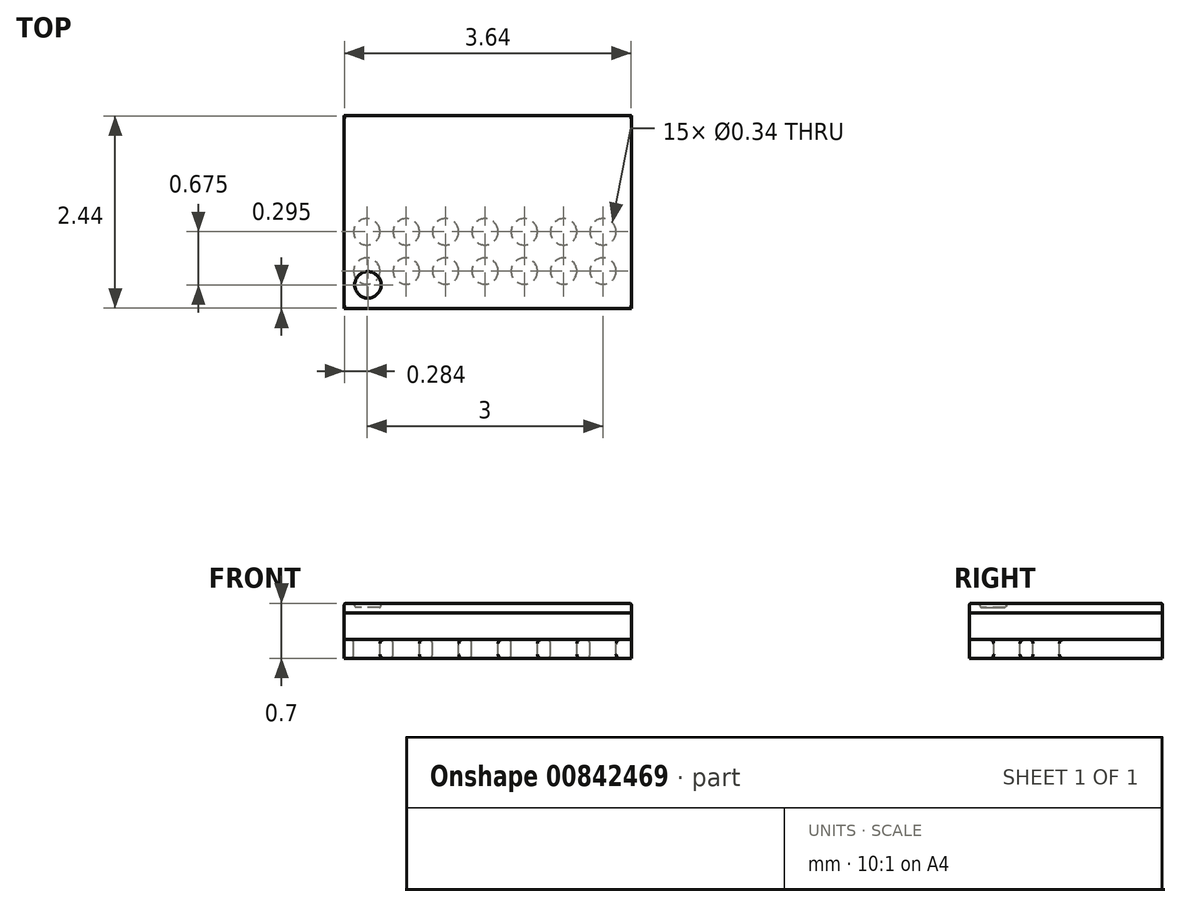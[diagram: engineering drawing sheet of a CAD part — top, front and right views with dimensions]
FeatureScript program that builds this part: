
annotation { "Feature Type Name" : "Feature", "Feature Type Description" : "" }
export const myFeature = defineFeature(function(context is Context, id is Id, definition is map)
    precondition{}
    {
        {
            var Q0;
            Q0=qCreatedBy(makeId("Top.planeOp"),FACE);
            var sketch = newSketch(context, id + "F0", { "sketchPlane" : qUnion([Q0])});
            skLineSegment(sketch, "E0.bottom", {"start": v(-1.82, 1.22) * mm, "end": v(1.82, 1.22) * mm});
            skLineSegment(sketch, "E0.top", {"start": v(-1.82, -1.22) * mm, "end": v(1.82, -1.22) * mm});
            skLineSegment(sketch, "E0.left", {"start": v(-1.82, 1.22) * mm, "end": v(-1.82, -1.22) * mm});
            skLineSegment(sketch, "E0.right", {"start": v(1.82, 1.22) * mm, "end": v(1.82, -1.22) * mm});
            skPoint(sketch, "E0.middle", {"position": v(0, 0) * mm});
            skSolve(sketch);
        }
        {
            var Q0;
            Q0=makeQuery(id+"F0.imprint","IMPRINT",FACE,{"disambiguationData":[TD([[makeQuery(id+"F0.imprint","IMPRINT",EDGE,{"derivedFrom":sQuery(id+"F0.wireOp",EDGE,"E0.bottom")}),-1.0]])]});
            extrude(context, id + "F1", {"entities" : qUnion([Q0]), "depth" : 0.34 * mm, "offsetDistance" : 25 * mm});
        }
        {
            var Q0;
            Q0=makeQuery(id+"F1.opExtrude","CAP_FACE",FACE,{"disambiguationData":[OSD([sQuery(id+"F0.wireOp",EDGE,"E0.bottom"),sQuery(id+"F0.wireOp",EDGE,"E0.top"),sQuery(id+"F0.wireOp",EDGE,"E0.left"),sQuery(id+"F0.wireOp",EDGE,"E0.right")])],"isStart":false});
            extrude(context, id + "F2", {"entities" : qUnion([Q0]), "depth" : 0.12 * mm, "offsetDistance" : 25 * mm});
        }
        {
            var Q0;
            Q0=makeQuery(id+"F1.opExtrude","CAP_FACE",FACE,{"disambiguationData":[OSD([sQuery(id+"F0.wireOp",EDGE,"E0.bottom"),sQuery(id+"F0.wireOp",EDGE,"E0.top"),sQuery(id+"F0.wireOp",EDGE,"E0.left"),sQuery(id+"F0.wireOp",EDGE,"E0.right")])],"isStart":true});
            var sketch = newSketch(context, id + "F3", { "sketchPlane" : qUnion([Q0])});
            skCircle(sketch, "E1", {"center": v(1.46, -0.75) * mm, "radius": 0.17 * mm});
            skCircle(sketch, "E2", {"center": v(1.46, -0.25) * mm, "radius": 0.17 * mm});
            skCircle(sketch, "E3", {"center": v(0.96, -0.75) * mm, "radius": 0.17 * mm});
            skCircle(sketch, "E4", {"center": v(0.96, -0.25) * mm, "radius": 0.17 * mm});
            skCircle(sketch, "E5", {"center": v(0.46, -0.75) * mm, "radius": 0.17 * mm});
            skCircle(sketch, "E6", {"center": v(0.46, -0.25) * mm, "radius": 0.17 * mm});
            skCircle(sketch, "E7", {"center": v(-0.04, -0.75) * mm, "radius": 0.17 * mm});
            skCircle(sketch, "E8", {"center": v(-0.04, -0.25) * mm, "radius": 0.17 * mm});
            skCircle(sketch, "E9", {"center": v(-0.54, -0.75) * mm, "radius": 0.17 * mm});
            skCircle(sketch, "E10", {"center": v(-0.54, -0.25) * mm, "radius": 0.17 * mm});
            skCircle(sketch, "E11", {"center": v(-1.04, -0.75) * mm, "radius": 0.17 * mm});
            skCircle(sketch, "E12", {"center": v(-1.04, -0.25) * mm, "radius": 0.17 * mm});
            skCircle(sketch, "E13", {"center": v(-1.54, -0.75) * mm, "radius": 0.17 * mm});
            skCircle(sketch, "E14", {"center": v(-1.54, -0.25) * mm, "radius": 0.17 * mm});
            skCircle(sketch, "E15.MirrorC", {"center": v(-1.54, 0.25) * mm, "radius": 0.17 * mm});
            skCircle(sketch, "E16.MirrorC", {"center": v(-1.04, 0.25) * mm, "radius": 0.17 * mm});
            skCircle(sketch, "E17.MirrorC", {"center": v(-0.54, 0.25) * mm, "radius": 0.17 * mm});
            skCircle(sketch, "E18.MirrorC", {"center": v(-0.04, 0.25) * mm, "radius": 0.17 * mm});
            skCircle(sketch, "E19.MirrorC", {"center": v(0.46, 0.25) * mm, "radius": 0.17 * mm});
            skCircle(sketch, "E20.MirrorC", {"center": v(0.96, 0.25) * mm, "radius": 0.17 * mm});
            skCircle(sketch, "E21.MirrorC", {"center": v(1.46, 0.25) * mm, "radius": 0.17 * mm});
            skCircle(sketch, "E22.MirrorC", {"center": v(1.46, 0.75) * mm, "radius": 0.17 * mm});
            skCircle(sketch, "E23.MirrorC", {"center": v(0.96, 0.75) * mm, "radius": 0.17 * mm});
            skCircle(sketch, "E24.MirrorC", {"center": v(0.46, 0.75) * mm, "radius": 0.17 * mm});
            skCircle(sketch, "E25.MirrorC", {"center": v(-0.04, 0.75) * mm, "radius": 0.17 * mm});
            skCircle(sketch, "E26.MirrorC", {"center": v(-0.54, 0.75) * mm, "radius": 0.17 * mm});
            skCircle(sketch, "E27.MirrorC", {"center": v(-1.04, 0.75) * mm, "radius": 0.17 * mm});
            skCircle(sketch, "E28.MirrorC", {"center": v(-1.54, 0.75) * mm, "radius": 0.17 * mm});
            skSolve(sketch);
        }
        {
            var Q0;
            Q0=makeQuery(id+"F3.imprint","IMPRINT",FACE,{"disambiguationData":[TD([[makeQuery(id+"F3.imprint","IMPRINT",EDGE,{"derivedFrom":sQuery(id+"F3.wireOp",EDGE,"E1")}),1.0]])]});
            var Q1;
            Q1=makeQuery(id+"F3.imprint","IMPRINT",FACE,{"disambiguationData":[TD([[makeQuery(id+"F3.imprint","IMPRINT",EDGE,{"derivedFrom":sQuery(id+"F3.wireOp",EDGE,"E2")}),1.0]])]});
            var Q2;
            Q2=makeQuery(id+"F3.imprint","IMPRINT",FACE,{"disambiguationData":[TD([[makeQuery(id+"F3.imprint","IMPRINT",EDGE,{"derivedFrom":sQuery(id+"F3.wireOp",EDGE,"E3")}),1.0]])]});
            var Q3;
            Q3=makeQuery(id+"F3.imprint","IMPRINT",FACE,{"disambiguationData":[TD([[makeQuery(id+"F3.imprint","IMPRINT",EDGE,{"derivedFrom":sQuery(id+"F3.wireOp",EDGE,"E4")}),1.0]])]});
            var Q4;
            Q4=makeQuery(id+"F3.imprint","IMPRINT",FACE,{"disambiguationData":[TD([[makeQuery(id+"F3.imprint","IMPRINT",EDGE,{"derivedFrom":sQuery(id+"F3.wireOp",EDGE,"E5")}),1.0]])]});
            var Q5;
            Q5=makeQuery(id+"F3.imprint","IMPRINT",FACE,{"disambiguationData":[TD([[makeQuery(id+"F3.imprint","IMPRINT",EDGE,{"derivedFrom":sQuery(id+"F3.wireOp",EDGE,"E6")}),1.0]])]});
            var Q6;
            Q6=makeQuery(id+"F3.imprint","IMPRINT",FACE,{"disambiguationData":[TD([[makeQuery(id+"F3.imprint","IMPRINT",EDGE,{"derivedFrom":sQuery(id+"F3.wireOp",EDGE,"E7")}),1.0]])]});
            var Q7;
            Q7=makeQuery(id+"F3.imprint","IMPRINT",FACE,{"disambiguationData":[TD([[makeQuery(id+"F3.imprint","IMPRINT",EDGE,{"derivedFrom":sQuery(id+"F3.wireOp",EDGE,"E8")}),1.0]])]});
            var Q8;
            Q8=makeQuery(id+"F3.imprint","IMPRINT",FACE,{"disambiguationData":[TD([[makeQuery(id+"F3.imprint","IMPRINT",EDGE,{"derivedFrom":sQuery(id+"F3.wireOp",EDGE,"E9")}),1.0]])]});
            var Q9;
            Q9=makeQuery(id+"F3.imprint","IMPRINT",FACE,{"disambiguationData":[TD([[makeQuery(id+"F3.imprint","IMPRINT",EDGE,{"derivedFrom":sQuery(id+"F3.wireOp",EDGE,"E10")}),1.0]])]});
            var Q10;
            Q10=makeQuery(id+"F3.imprint","IMPRINT",FACE,{"disambiguationData":[TD([[makeQuery(id+"F3.imprint","IMPRINT",EDGE,{"derivedFrom":sQuery(id+"F3.wireOp",EDGE,"E11")}),1.0]])]});
            var Q11;
            Q11=makeQuery(id+"F3.imprint","IMPRINT",FACE,{"disambiguationData":[TD([[makeQuery(id+"F3.imprint","IMPRINT",EDGE,{"derivedFrom":sQuery(id+"F3.wireOp",EDGE,"E12")}),1.0]])]});
            var Q12;
            Q12=makeQuery(id+"F3.imprint","IMPRINT",FACE,{"disambiguationData":[TD([[makeQuery(id+"F3.imprint","IMPRINT",EDGE,{"derivedFrom":sQuery(id+"F3.wireOp",EDGE,"E13")}),1.0]])]});
            var Q13;
            Q13=makeQuery(id+"F3.imprint","IMPRINT",FACE,{"disambiguationData":[TD([[makeQuery(id+"F3.imprint","IMPRINT",EDGE,{"derivedFrom":sQuery(id+"F3.wireOp",EDGE,"E14")}),1.0]])]});
            var Q14;
            Q14=makeQuery(id+"F3.imprint","IMPRINT",FACE,{"disambiguationData":[TD([[makeQuery(id+"F3.imprint","IMPRINT",EDGE,{"derivedFrom":sQuery(id+"F3.wireOp",EDGE,"E15.MirrorC")}),-1.0]])]});
            var Q15;
            Q15=makeQuery(id+"F3.imprint","IMPRINT",FACE,{"disambiguationData":[TD([[makeQuery(id+"F3.imprint","IMPRINT",EDGE,{"derivedFrom":sQuery(id+"F3.wireOp",EDGE,"E28.MirrorC")}),-1.0]])]});
            var Q16;
            Q16=makeQuery(id+"F3.imprint","IMPRINT",FACE,{"disambiguationData":[TD([[makeQuery(id+"F3.imprint","IMPRINT",EDGE,{"derivedFrom":sQuery(id+"F3.wireOp",EDGE,"E27.MirrorC")}),-1.0]])]});
            var Q17;
            Q17=makeQuery(id+"F3.imprint","IMPRINT",FACE,{"disambiguationData":[TD([[makeQuery(id+"F3.imprint","IMPRINT",EDGE,{"derivedFrom":sQuery(id+"F3.wireOp",EDGE,"E16.MirrorC")}),-1.0]])]});
            var Q18;
            Q18=makeQuery(id+"F3.imprint","IMPRINT",FACE,{"disambiguationData":[TD([[makeQuery(id+"F3.imprint","IMPRINT",EDGE,{"derivedFrom":sQuery(id+"F3.wireOp",EDGE,"E17.MirrorC")}),-1.0]])]});
            var Q19;
            Q19=makeQuery(id+"F3.imprint","IMPRINT",FACE,{"disambiguationData":[TD([[makeQuery(id+"F3.imprint","IMPRINT",EDGE,{"derivedFrom":sQuery(id+"F3.wireOp",EDGE,"E26.MirrorC")}),-1.0]])]});
            var Q20;
            Q20=makeQuery(id+"F3.imprint","IMPRINT",FACE,{"disambiguationData":[TD([[makeQuery(id+"F3.imprint","IMPRINT",EDGE,{"derivedFrom":sQuery(id+"F3.wireOp",EDGE,"E25.MirrorC")}),-1.0]])]});
            var Q21;
            Q21=makeQuery(id+"F3.imprint","IMPRINT",FACE,{"disambiguationData":[TD([[makeQuery(id+"F3.imprint","IMPRINT",EDGE,{"derivedFrom":sQuery(id+"F3.wireOp",EDGE,"E18.MirrorC")}),-1.0]])]});
            var Q22;
            Q22=makeQuery(id+"F3.imprint","IMPRINT",FACE,{"disambiguationData":[TD([[makeQuery(id+"F3.imprint","IMPRINT",EDGE,{"derivedFrom":sQuery(id+"F3.wireOp",EDGE,"E19.MirrorC")}),-1.0]])]});
            var Q23;
            Q23=makeQuery(id+"F3.imprint","IMPRINT",FACE,{"disambiguationData":[TD([[makeQuery(id+"F3.imprint","IMPRINT",EDGE,{"derivedFrom":sQuery(id+"F3.wireOp",EDGE,"E24.MirrorC")}),-1.0]])]});
            var Q24;
            Q24=makeQuery(id+"F3.imprint","IMPRINT",FACE,{"disambiguationData":[TD([[makeQuery(id+"F3.imprint","IMPRINT",EDGE,{"derivedFrom":sQuery(id+"F3.wireOp",EDGE,"E23.MirrorC")}),-1.0]])]});
            var Q25;
            Q25=makeQuery(id+"F3.imprint","IMPRINT",FACE,{"disambiguationData":[TD([[makeQuery(id+"F3.imprint","IMPRINT",EDGE,{"derivedFrom":sQuery(id+"F3.wireOp",EDGE,"E20.MirrorC")}),-1.0]])]});
            var Q26;
            Q26=makeQuery(id+"F3.imprint","IMPRINT",FACE,{"disambiguationData":[TD([[makeQuery(id+"F3.imprint","IMPRINT",EDGE,{"derivedFrom":sQuery(id+"F3.wireOp",EDGE,"E21.MirrorC")}),-1.0]])]});
            var Q27;
            Q27=makeQuery(id+"F3.imprint","IMPRINT",FACE,{"disambiguationData":[TD([[makeQuery(id+"F3.imprint","IMPRINT",EDGE,{"derivedFrom":sQuery(id+"F3.wireOp",EDGE,"E22.MirrorC")}),-1.0]])]});
            extrude(context, id + "F4", {"entities" : qUnion([Q0, Q1, Q2, Q3, Q4, Q5, Q6, Q7, Q8, Q9, Q10, Q11, Q12, Q13, Q14, Q15, Q16, Q17, Q18, Q19, Q20, Q21, Q22, Q23, Q24, Q25, Q26, Q27]), "depth" : 0.24 * mm, "offsetDistance" : 25 * mm});
        }
        {
            var Q0;
            Q0=makeQuery(id+"F4.opExtrude","CAP_EDGE",EDGE,{"disambiguationData":[OSD([sQuery(id+"F3.wireOp",EDGE,"E28.MirrorC")])],"isStart":false});
            var Q1;
            Q1=makeQuery(id+"F4.opExtrude","CAP_EDGE",EDGE,{"disambiguationData":[OSD([sQuery(id+"F3.wireOp",EDGE,"E27.MirrorC")])],"isStart":false});
            var Q2;
            Q2=makeQuery(id+"F4.opExtrude","CAP_EDGE",EDGE,{"disambiguationData":[OSD([sQuery(id+"F3.wireOp",EDGE,"E26.MirrorC")])],"isStart":false});
            var Q3;
            Q3=makeQuery(id+"F4.opExtrude","CAP_EDGE",EDGE,{"disambiguationData":[OSD([sQuery(id+"F3.wireOp",EDGE,"E24.MirrorC")])],"isStart":false});
            var Q4;
            Q4=makeQuery(id+"F4.opExtrude","CAP_EDGE",EDGE,{"disambiguationData":[OSD([sQuery(id+"F3.wireOp",EDGE,"E23.MirrorC")])],"isStart":false});
            var Q5;
            Q5=makeQuery(id+"F4.opExtrude","CAP_EDGE",EDGE,{"disambiguationData":[OSD([sQuery(id+"F3.wireOp",EDGE,"E25.MirrorC")])],"isStart":false});
            var Q6;
            Q6=makeQuery(id+"F4.opExtrude","CAP_EDGE",EDGE,{"disambiguationData":[OSD([sQuery(id+"F3.wireOp",EDGE,"E22.MirrorC")])],"isStart":false});
            var Q7;
            Q7=makeQuery(id+"F4.opExtrude","CAP_EDGE",EDGE,{"disambiguationData":[OSD([sQuery(id+"F3.wireOp",EDGE,"E21.MirrorC")])],"isStart":false});
            var Q8;
            Q8=makeQuery(id+"F4.opExtrude","CAP_EDGE",EDGE,{"disambiguationData":[OSD([sQuery(id+"F3.wireOp",EDGE,"E20.MirrorC")])],"isStart":false});
            var Q9;
            Q9=makeQuery(id+"F4.opExtrude","CAP_EDGE",EDGE,{"disambiguationData":[OSD([sQuery(id+"F3.wireOp",EDGE,"E19.MirrorC")])],"isStart":false});
            var Q10;
            Q10=makeQuery(id+"F4.opExtrude","CAP_EDGE",EDGE,{"disambiguationData":[OSD([sQuery(id+"F3.wireOp",EDGE,"E18.MirrorC")])],"isStart":false});
            var Q11;
            Q11=makeQuery(id+"F4.opExtrude","CAP_EDGE",EDGE,{"disambiguationData":[OSD([sQuery(id+"F3.wireOp",EDGE,"E17.MirrorC")])],"isStart":false});
            var Q12;
            Q12=makeQuery(id+"F4.opExtrude","CAP_EDGE",EDGE,{"disambiguationData":[OSD([sQuery(id+"F3.wireOp",EDGE,"E16.MirrorC")])],"isStart":false});
            var Q13;
            Q13=makeQuery(id+"F4.opExtrude","CAP_EDGE",EDGE,{"disambiguationData":[OSD([sQuery(id+"F3.wireOp",EDGE,"E15.MirrorC")])],"isStart":false});
            var Q14;
            Q14=makeQuery(id+"F4.opExtrude","CAP_EDGE",EDGE,{"disambiguationData":[OSD([sQuery(id+"F3.wireOp",EDGE,"E14")])],"isStart":false});
            var Q15;
            Q15=makeQuery(id+"F4.opExtrude","CAP_EDGE",EDGE,{"disambiguationData":[OSD([sQuery(id+"F3.wireOp",EDGE,"E12")])],"isStart":false});
            var Q16;
            Q16=makeQuery(id+"F4.opExtrude","CAP_EDGE",EDGE,{"disambiguationData":[OSD([sQuery(id+"F3.wireOp",EDGE,"E10")])],"isStart":false});
            var Q17;
            Q17=makeQuery(id+"F4.opExtrude","CAP_EDGE",EDGE,{"disambiguationData":[OSD([sQuery(id+"F3.wireOp",EDGE,"E8")])],"isStart":false});
            var Q18;
            Q18=makeQuery(id+"F4.opExtrude","CAP_EDGE",EDGE,{"disambiguationData":[OSD([sQuery(id+"F3.wireOp",EDGE,"E6")])],"isStart":false});
            var Q19;
            Q19=makeQuery(id+"F4.opExtrude","CAP_EDGE",EDGE,{"disambiguationData":[OSD([sQuery(id+"F3.wireOp",EDGE,"E4")])],"isStart":false});
            var Q20;
            Q20=makeQuery(id+"F4.opExtrude","CAP_EDGE",EDGE,{"disambiguationData":[OSD([sQuery(id+"F3.wireOp",EDGE,"E2")])],"isStart":false});
            var Q21;
            Q21=makeQuery(id+"F4.opExtrude","CAP_EDGE",EDGE,{"disambiguationData":[OSD([sQuery(id+"F3.wireOp",EDGE,"E13")])],"isStart":false});
            var Q22;
            Q22=makeQuery(id+"F4.opExtrude","CAP_EDGE",EDGE,{"disambiguationData":[OSD([sQuery(id+"F3.wireOp",EDGE,"E11")])],"isStart":false});
            var Q23;
            Q23=makeQuery(id+"F4.opExtrude","CAP_EDGE",EDGE,{"disambiguationData":[OSD([sQuery(id+"F3.wireOp",EDGE,"E13")])],"isStart":true});
            var Q24;
            Q24=makeQuery(id+"F4.opExtrude","CAP_EDGE",EDGE,{"disambiguationData":[OSD([sQuery(id+"F3.wireOp",EDGE,"E11")])],"isStart":true});
            var Q25;
            Q25=makeQuery(id+"F4.opExtrude","CAP_EDGE",EDGE,{"disambiguationData":[OSD([sQuery(id+"F3.wireOp",EDGE,"E9")])],"isStart":false});
            var Q26;
            Q26=makeQuery(id+"F4.opExtrude","CAP_EDGE",EDGE,{"disambiguationData":[OSD([sQuery(id+"F3.wireOp",EDGE,"E9")])],"isStart":true});
            var Q27;
            Q27=makeQuery(id+"F4.opExtrude","CAP_EDGE",EDGE,{"disambiguationData":[OSD([sQuery(id+"F3.wireOp",EDGE,"E7")])],"isStart":true});
            var Q28;
            Q28=makeQuery(id+"F4.opExtrude","CAP_EDGE",EDGE,{"disambiguationData":[OSD([sQuery(id+"F3.wireOp",EDGE,"E7")])],"isStart":false});
            var Q29;
            Q29=makeQuery(id+"F4.opExtrude","CAP_EDGE",EDGE,{"disambiguationData":[OSD([sQuery(id+"F3.wireOp",EDGE,"E5")])],"isStart":true});
            var Q30;
            Q30=makeQuery(id+"F4.opExtrude","CAP_EDGE",EDGE,{"disambiguationData":[OSD([sQuery(id+"F3.wireOp",EDGE,"E5")])],"isStart":false});
            var Q31;
            Q31=makeQuery(id+"F4.opExtrude","CAP_EDGE",EDGE,{"disambiguationData":[OSD([sQuery(id+"F3.wireOp",EDGE,"E3")])],"isStart":false});
            var Q32;
            Q32=makeQuery(id+"F4.opExtrude","CAP_EDGE",EDGE,{"disambiguationData":[OSD([sQuery(id+"F3.wireOp",EDGE,"E3")])],"isStart":true});
            var Q33;
            Q33=makeQuery(id+"F4.opExtrude","CAP_EDGE",EDGE,{"disambiguationData":[OSD([sQuery(id+"F3.wireOp",EDGE,"E1")])],"isStart":false});
            var Q34;
            Q34=makeQuery(id+"F4.opExtrude","CAP_EDGE",EDGE,{"disambiguationData":[OSD([sQuery(id+"F3.wireOp",EDGE,"E1")])],"isStart":true});
            var Q35;
            Q35=makeQuery(id+"F4.opExtrude","CAP_EDGE",EDGE,{"disambiguationData":[OSD([sQuery(id+"F3.wireOp",EDGE,"E2")])],"isStart":true});
            var Q36;
            Q36=makeQuery(id+"F4.opExtrude","CAP_EDGE",EDGE,{"disambiguationData":[OSD([sQuery(id+"F3.wireOp",EDGE,"E4")])],"isStart":true});
            var Q37;
            Q37=makeQuery(id+"F4.opExtrude","CAP_EDGE",EDGE,{"disambiguationData":[OSD([sQuery(id+"F3.wireOp",EDGE,"E6")])],"isStart":true});
            var Q38;
            Q38=makeQuery(id+"F4.opExtrude","CAP_EDGE",EDGE,{"disambiguationData":[OSD([sQuery(id+"F3.wireOp",EDGE,"E8")])],"isStart":true});
            var Q39;
            Q39=makeQuery(id+"F4.opExtrude","CAP_EDGE",EDGE,{"disambiguationData":[OSD([sQuery(id+"F3.wireOp",EDGE,"E10")])],"isStart":true});
            var Q40;
            Q40=makeQuery(id+"F4.opExtrude","CAP_EDGE",EDGE,{"disambiguationData":[OSD([sQuery(id+"F3.wireOp",EDGE,"E12")])],"isStart":true});
            var Q41;
            Q41=makeQuery(id+"F4.opExtrude","CAP_EDGE",EDGE,{"disambiguationData":[OSD([sQuery(id+"F3.wireOp",EDGE,"E14")])],"isStart":true});
            var Q42;
            Q42=makeQuery(id+"F4.opExtrude","CAP_EDGE",EDGE,{"disambiguationData":[OSD([sQuery(id+"F3.wireOp",EDGE,"E15.MirrorC")])],"isStart":true});
            var Q43;
            Q43=makeQuery(id+"F4.opExtrude","CAP_EDGE",EDGE,{"disambiguationData":[OSD([sQuery(id+"F3.wireOp",EDGE,"E28.MirrorC")])],"isStart":true});
            var Q44;
            Q44=makeQuery(id+"F4.opExtrude","CAP_EDGE",EDGE,{"disambiguationData":[OSD([sQuery(id+"F3.wireOp",EDGE,"E16.MirrorC")])],"isStart":true});
            var Q45;
            Q45=makeQuery(id+"F4.opExtrude","CAP_EDGE",EDGE,{"disambiguationData":[OSD([sQuery(id+"F3.wireOp",EDGE,"E27.MirrorC")])],"isStart":true});
            var Q46;
            Q46=makeQuery(id+"F4.opExtrude","CAP_EDGE",EDGE,{"disambiguationData":[OSD([sQuery(id+"F3.wireOp",EDGE,"E26.MirrorC")])],"isStart":true});
            var Q47;
            Q47=makeQuery(id+"F4.opExtrude","CAP_EDGE",EDGE,{"disambiguationData":[OSD([sQuery(id+"F3.wireOp",EDGE,"E17.MirrorC")])],"isStart":true});
            var Q48;
            Q48=makeQuery(id+"F4.opExtrude","CAP_EDGE",EDGE,{"disambiguationData":[OSD([sQuery(id+"F3.wireOp",EDGE,"E25.MirrorC")])],"isStart":true});
            var Q49;
            Q49=makeQuery(id+"F4.opExtrude","CAP_EDGE",EDGE,{"disambiguationData":[OSD([sQuery(id+"F3.wireOp",EDGE,"E18.MirrorC")])],"isStart":true});
            var Q50;
            Q50=makeQuery(id+"F4.opExtrude","CAP_EDGE",EDGE,{"disambiguationData":[OSD([sQuery(id+"F3.wireOp",EDGE,"E19.MirrorC")])],"isStart":true});
            var Q51;
            Q51=makeQuery(id+"F4.opExtrude","CAP_EDGE",EDGE,{"disambiguationData":[OSD([sQuery(id+"F3.wireOp",EDGE,"E24.MirrorC")])],"isStart":true});
            var Q52;
            Q52=makeQuery(id+"F4.opExtrude","CAP_EDGE",EDGE,{"disambiguationData":[OSD([sQuery(id+"F3.wireOp",EDGE,"E23.MirrorC")])],"isStart":true});
            var Q53;
            Q53=makeQuery(id+"F4.opExtrude","CAP_EDGE",EDGE,{"disambiguationData":[OSD([sQuery(id+"F3.wireOp",EDGE,"E20.MirrorC")])],"isStart":true});
            var Q54;
            Q54=makeQuery(id+"F4.opExtrude","CAP_EDGE",EDGE,{"disambiguationData":[OSD([sQuery(id+"F3.wireOp",EDGE,"E22.MirrorC")])],"isStart":true});
            var Q55;
            Q55=makeQuery(id+"F4.opExtrude","CAP_EDGE",EDGE,{"disambiguationData":[OSD([sQuery(id+"F3.wireOp",EDGE,"E21.MirrorC")])],"isStart":true});
            fillet(context, id + "F5", {"entities" : qUnion([Q0, Q1, Q2, Q3, Q4, Q5, Q6, Q7, Q8, Q9, Q10, Q11, Q12, Q13, Q14, Q15, Q16, Q17, Q18, Q19, Q20, Q21, Q22, Q23, Q24, Q25, Q26, Q27, Q28, Q29, Q30, Q31, Q32, Q33, Q34, Q35, Q36, Q37, Q38, Q39, Q40, Q41, Q42, Q43, Q44, Q45, Q46, Q47, Q48, Q49, Q50, Q51, Q52, Q53, Q54, Q55]), "radius" : 0.05 * mm, "tangentPropagation" : true, "allowEdgeOverflow" : false});
        }
        {
            var Q0;
            Q0=makeQuery(id+"F2.opExtrude","CAP_FACE",FACE,{"disambiguationData":[OSD([sQuery(id+"F0.wireOp",EDGE,"E0.bottom"),sQuery(id+"F0.wireOp",EDGE,"E0.top"),sQuery(id+"F0.wireOp",EDGE,"E0.left"),sQuery(id+"F0.wireOp",EDGE,"E0.right")])],"isStart":false});
            var sketch = newSketch(context, id + "F6", { "sketchPlane" : qUnion([Q0])});
            skCircle(sketch, "E29", {"center": v(-1.52, -0.92) * mm, "radius": 0.17 * mm});
            skSolve(sketch);
        }
        {
            var Q0;
            Q0=makeQuery(id+"F6.imprint","IMPRINT",FACE,{"disambiguationData":[TD([[makeQuery(id+"F6.imprint","IMPRINT",EDGE,{"derivedFrom":sQuery(id+"F6.wireOp",EDGE,"E29")}),1.0]])]});
            extrude(context, id + "F7", {"entities" : qUnion([Q0]), "operationType" : NewBodyOperationType.REMOVE, "oppositeDirection" : true, "depth" : 0.05 * mm, "offsetDistance" : 25 * mm});
        }
        {
            var Q0;
            Q0=makeQuery(id+"F7.boolean.opBoolean","COPY",EDGE,{"derivedFrom":makeQuery(id+"F7.opExtrude","CAP_EDGE",EDGE,{"disambiguationData":[OSD([sQuery(id+"F6.wireOp",EDGE,"E29")])],"isStart":true})});
            var Q1;
            Q1=makeQuery(id+"F2.opExtrude","CAP_FACE",FACE,{"disambiguationData":[OSD([sQuery(id+"F0.wireOp",EDGE,"E0.bottom"),sQuery(id+"F0.wireOp",EDGE,"E0.top"),sQuery(id+"F0.wireOp",EDGE,"E0.left"),sQuery(id+"F0.wireOp",EDGE,"E0.right")])],"isStart":false});
            var Q2;
            Q2=makeQuery(id+"F7.boolean.opBoolean","COPY",FACE,{"derivedFrom":makeQuery(id+"F7.opExtrude","CAP_FACE",FACE,{"disambiguationData":[OSD([sQuery(id+"F6.wireOp",EDGE,"E29")])],"isStart":false})});
            fillet(context, id + "F8", {"entities" : qUnion([Q0, Q1, Q2]), "radius" : 0.02 * mm, "tangentPropagation" : true, "allowEdgeOverflow" : false});
        }
    });
